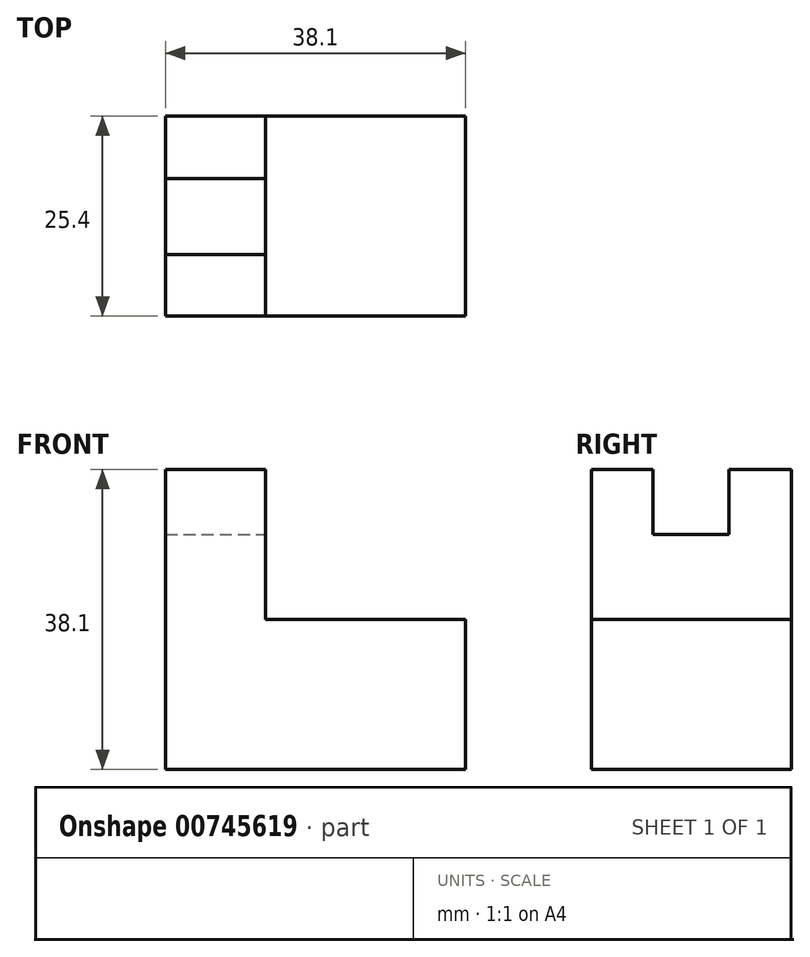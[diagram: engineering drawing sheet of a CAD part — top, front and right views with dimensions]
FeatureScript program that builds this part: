
annotation { "Feature Type Name" : "Feature", "Feature Type Description" : "" }
export const myFeature = defineFeature(function(context is Context, id is Id, definition is map)
    precondition{}
    {
        {
            var Q0;
            Q0=qCreatedBy(makeId("Front.planeOp"),FACE);
            var sketch = newSketch(context, id + "F0", { "sketchPlane" : qUnion([Q0])});
            skLineSegment(sketch, "E0", {"start": v(0, 0) * mm, "end": v(0, 38.1) * mm});
            skLineSegment(sketch, "E1", {"start": v(0, 0) * mm, "end": v(38.1, 0) * mm});
            skLineSegment(sketch, "E2", {"start": v(38.1, 0) * mm, "end": v(38.1, 19.05) * mm});
            skLineSegment(sketch, "E3", {"start": v(38.1, 19.05) * mm, "end": v(12.7, 19.05) * mm});
            skLineSegment(sketch, "E4", {"start": v(12.7, 19.05) * mm, "end": v(12.7, 38.1) * mm});
            skLineSegment(sketch, "E5", {"start": v(12.7, 38.1) * mm, "end": v(0, 38.1) * mm});
            skSolve(sketch);
        }
        {
            var Q0;
            Q0=makeQuery(id+"F0.imprint","IMPRINT",FACE,{"disambiguationData":[TD([[makeQuery(id+"F0.imprint","IMPRINT",EDGE,{"derivedFrom":sQuery(id+"F0.wireOp",EDGE,"E0")}),-1.0]])]});
            extrude(context, id + "F1", {"entities" : qUnion([Q0]), "depth" : 25.4 * mm, "offsetDistance" : 25.4 * mm});
        }
        {
            var Q0;
            Q0=makeQuery(id+"F1.opExtrude","SWEPT_FACE",FACE,{"disambiguationData":[OSD([sQuery(id+"F0.wireOp",EDGE,"E4")])]});
            var sketch = newSketch(context, id + "F2", { "sketchPlane" : qUnion([Q0])});
            skLineSegment(sketch, "E6", {"start": v(-17.6, 38.1) * mm, "end": v(-17.6, 29.85) * mm});
            skLineSegment(sketch, "E7", {"start": v(-17.6, 29.85) * mm, "end": v(-7.94, 29.85) * mm});
            skLineSegment(sketch, "E8", {"start": v(-7.94, 29.85) * mm, "end": v(-7.94, 38.1) * mm});
            skLineSegment(sketch, "E9", {"start": v(-88.55, 16.99) * mm, "end": v(-88.55, 20.4) * mm});
            skSolve(sketch);
        }
        {
            var Q0;
            {var subQ0=sQuery(id+"F2.wireOp",EDGE,"E6");Q0=makeQuery(id+"F2.imprint","IMPRINT",FACE,{"disambiguationData":[TD([[makeQuery(id+"F2.imprint","IMPRINT",EDGE,{"derivedFrom":subQ0}),1.0]])]});}
            extrude(context, id + "F3", {"entities" : qUnion([Q0]), "operationType" : NewBodyOperationType.REMOVE, "oppositeDirection" : true, "depth" : 25.4 * mm, "offsetDistance" : 25.4 * mm});
        }
    });
